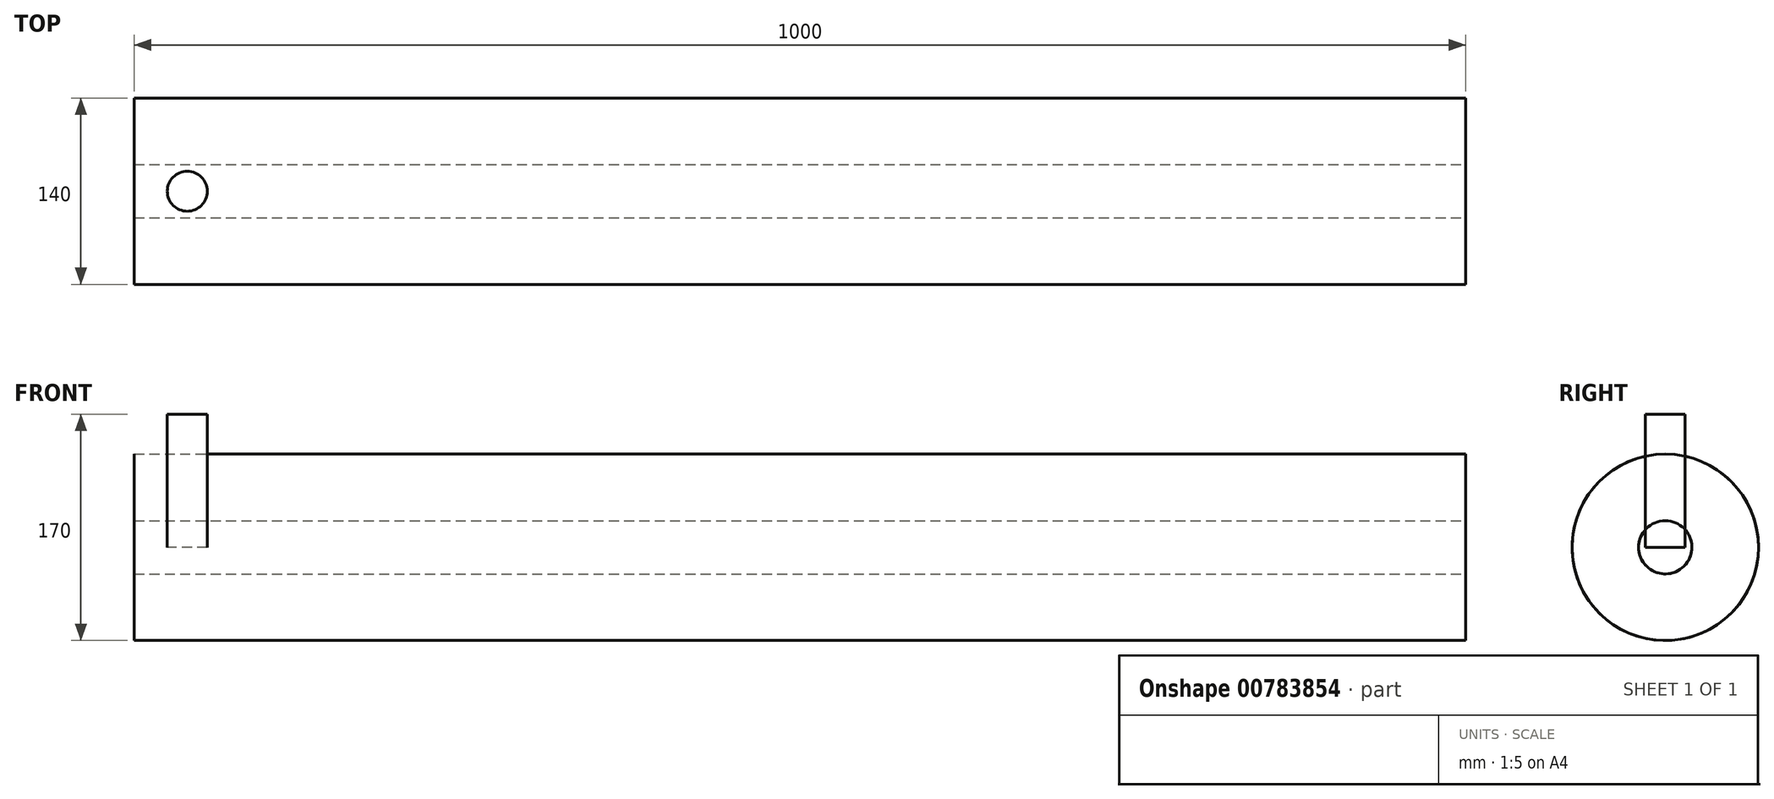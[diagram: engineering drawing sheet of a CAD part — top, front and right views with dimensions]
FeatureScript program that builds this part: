
annotation { "Feature Type Name" : "Feature", "Feature Type Description" : "" }
export const myFeature = defineFeature(function(context is Context, id is Id, definition is map)
    precondition{}
    {
        {
            var Q0;
            Q0=qCreatedBy(makeId("Right.planeOp"),FACE);
            var sketch = newSketch(context, id + "F0", { "sketchPlane" : qUnion([Q0])});
            skCircle(sketch, "E0", {"center": v(0, 0) * mm, "radius": 20 * mm});
            skSolve(sketch);
        }
        {
            var Q0;
            Q0=qCreatedBy(makeId("Right.planeOp"),FACE);
            var sketch = newSketch(context, id + "F1", { "sketchPlane" : qUnion([Q0])});
            skCircle(sketch, "E1", {"center": v(0, 0) * mm, "radius": 70 * mm});
            skSolve(sketch);
        }
        {
            var Q0;
            Q0=sQuery(id+"F1.wireOp",EDGE,"E1");
            var Q1;
            Q1=sQuery(id+"F0.wireOp",EDGE,"E0");
            extrude(context, id + "F2", {"bodyType" : ToolBodyType.SURFACE, "surfaceEntities" : qUnion([Q0, Q1]), "depth" : 1000 * mm, "offsetDistance" : 25 * mm});
        }
        {
            var Q0;
            Q0=qCreatedBy(makeId("Top.planeOp"),FACE);
            var sketch = newSketch(context, id + "F3", { "sketchPlane" : qUnion([Q0])});
            skCircle(sketch, "E2", {"center": v(39.84, 0) * mm, "radius": 15 * mm});
            skSolve(sketch);
        }
        {
            var Q0;
            Q0=sQuery(id+"F3.wireOp",EDGE,"E2");
            extrude(context, id + "F4", {"bodyType" : ToolBodyType.SURFACE, "surfaceEntities" : qUnion([Q0]), "depth" : 100 * mm, "offsetDistance" : 25 * mm});
        }
    });
